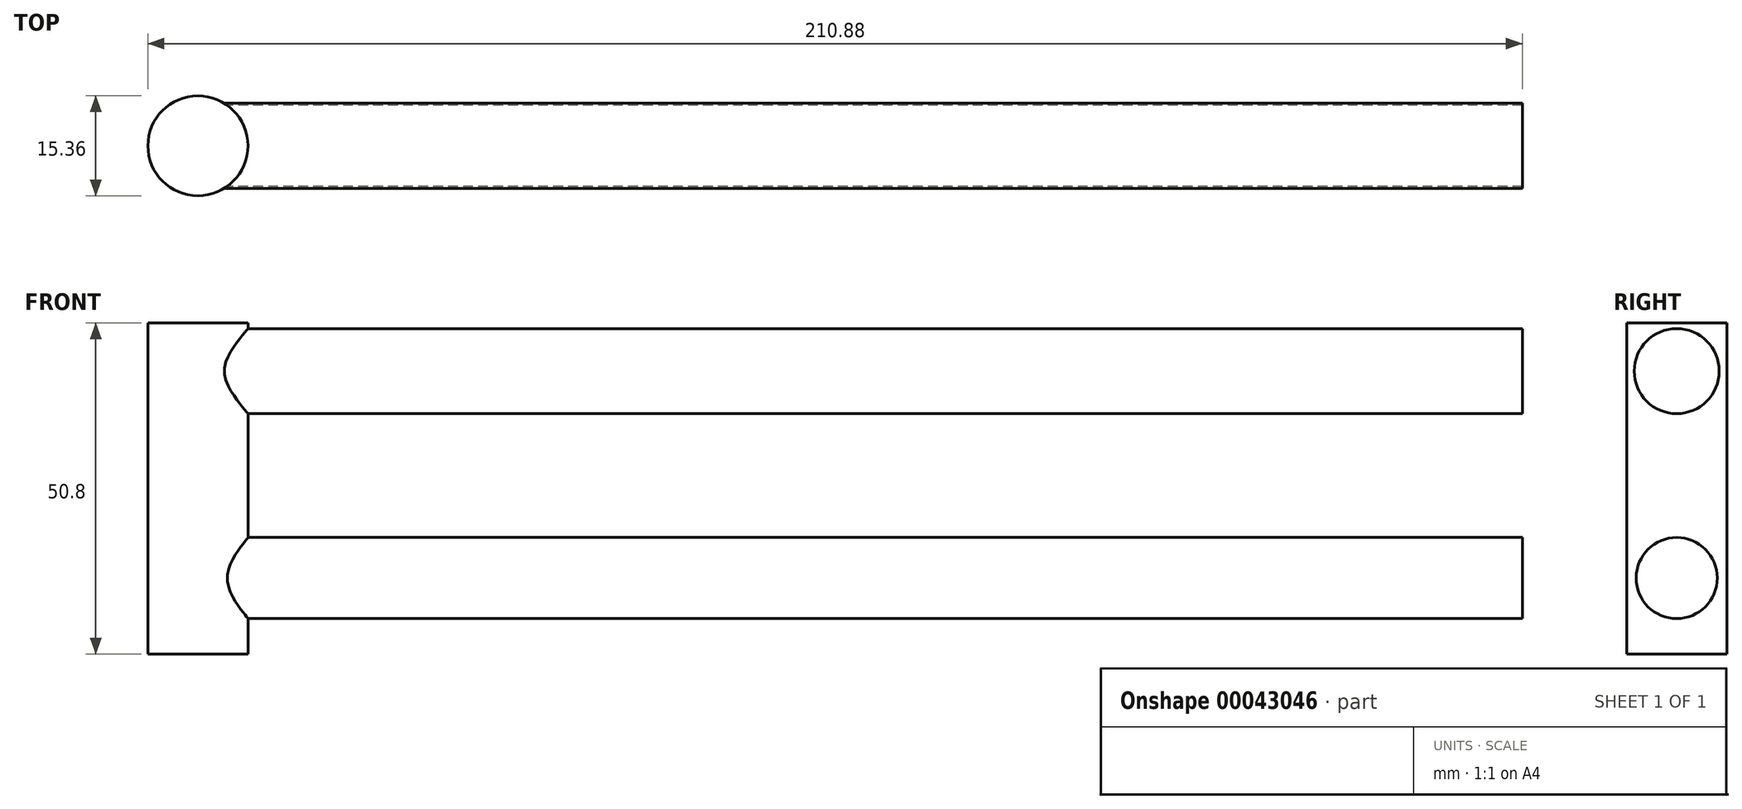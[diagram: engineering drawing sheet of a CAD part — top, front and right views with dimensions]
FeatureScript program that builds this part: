
annotation { "Feature Type Name" : "Feature", "Feature Type Description" : "" }
export const myFeature = defineFeature(function(context is Context, id is Id, definition is map)
    precondition{}
    {
        {
            var Q0;
            Q0=qCreatedBy(makeId("Top.planeOp"),FACE);
            var sketch = newSketch(context, id + "F0", { "sketchPlane" : qUnion([Q0])});
            skCircle(sketch, "E0", {"center": v(0, 0) * mm, "radius": 7.68 * mm});
            skSolve(sketch);
        }
        {
            var Q0;
            Q0 = qSketchRegion(id + "F0", true);
            extrude(context, id + "F1", {"entities" : qUnion([Q0]), "depth" : 50.8 * mm});
        }
        {
            var Q0;
            Q0=qCreatedBy(makeId("Right.planeOp"),FACE);
            var sketch = newSketch(context, id + "F2", { "sketchPlane" : qUnion([Q0])});
            skCircle(sketch, "E1", {"center": v(0, 43.41) * mm, "radius": 6.52 * mm});
            skSolve(sketch);
        }
        {
            var Q0;
            Q0 = qSketchRegion(id + "F2", true);
            extrude(context, id + "F3", {"entities" : qUnion([Q0]), "operationType" : NewBodyOperationType.ADD, "depth" : 203.2 * mm});
        }
        {
            var Q0;
            Q0=qCreatedBy(makeId("Right.planeOp"),FACE);
            var sketch = newSketch(context, id + "F4", { "sketchPlane" : qUnion([Q0])});
            skCircle(sketch, "E2", {"center": v(0, 11.66) * mm, "radius": 6.22 * mm});
            skSolve(sketch);
        }
        {
            var Q0;
            Q0 = qSketchRegion(id + "F4", true);
            extrude(context, id + "F5", {"entities" : qUnion([Q0]), "operationType" : NewBodyOperationType.ADD, "depth" : 203.2 * mm});
        }
    });
